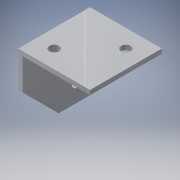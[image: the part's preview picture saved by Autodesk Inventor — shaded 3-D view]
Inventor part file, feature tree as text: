
AUTODESK INVENTOR PART (.ipt)
format: ipt  version: 2016 (Build 200138000, 138)  size: 122,368 bytes
history: native  units: in
note: dims shown in document units (in); Inventor stores cm internally (conversion verified against a paired STEP export)
features: extrude x3, sketch x3
ambient origin geometry x8: Origin, YZ Plane, XZ Plane, XY Plane, X Axis, Y Axis, Z Axis, Center Point
bodies: Solid1 (feature_tree)
feature tree (6):
  extrude  "Extrusion1"  Depth=0.125in
  sketch  "Sketch2"  dims[d2=1.875in d3=1.875in]
  extrude  "Extrusion4"  Depth=1.875in
  extrude  "Extrusion5"  Depth=0.125in
  sketch  "Sketch1"  dims[d0=2.0in d1=0.125in]
  sketch  "Sketch3"  dims[d4=2.0in d5=0.0in d13=1.5in d14=1.0in d15=0.5in d20=0.2656in d21=0.2656in d22=0.2656in d23=0.2656in d24=0.5in d25=0.5in d26=0.5in d27=0.375in d28=0.125in d29=0.0in d30=1.5in d31=0.125in d32=0.0in]
